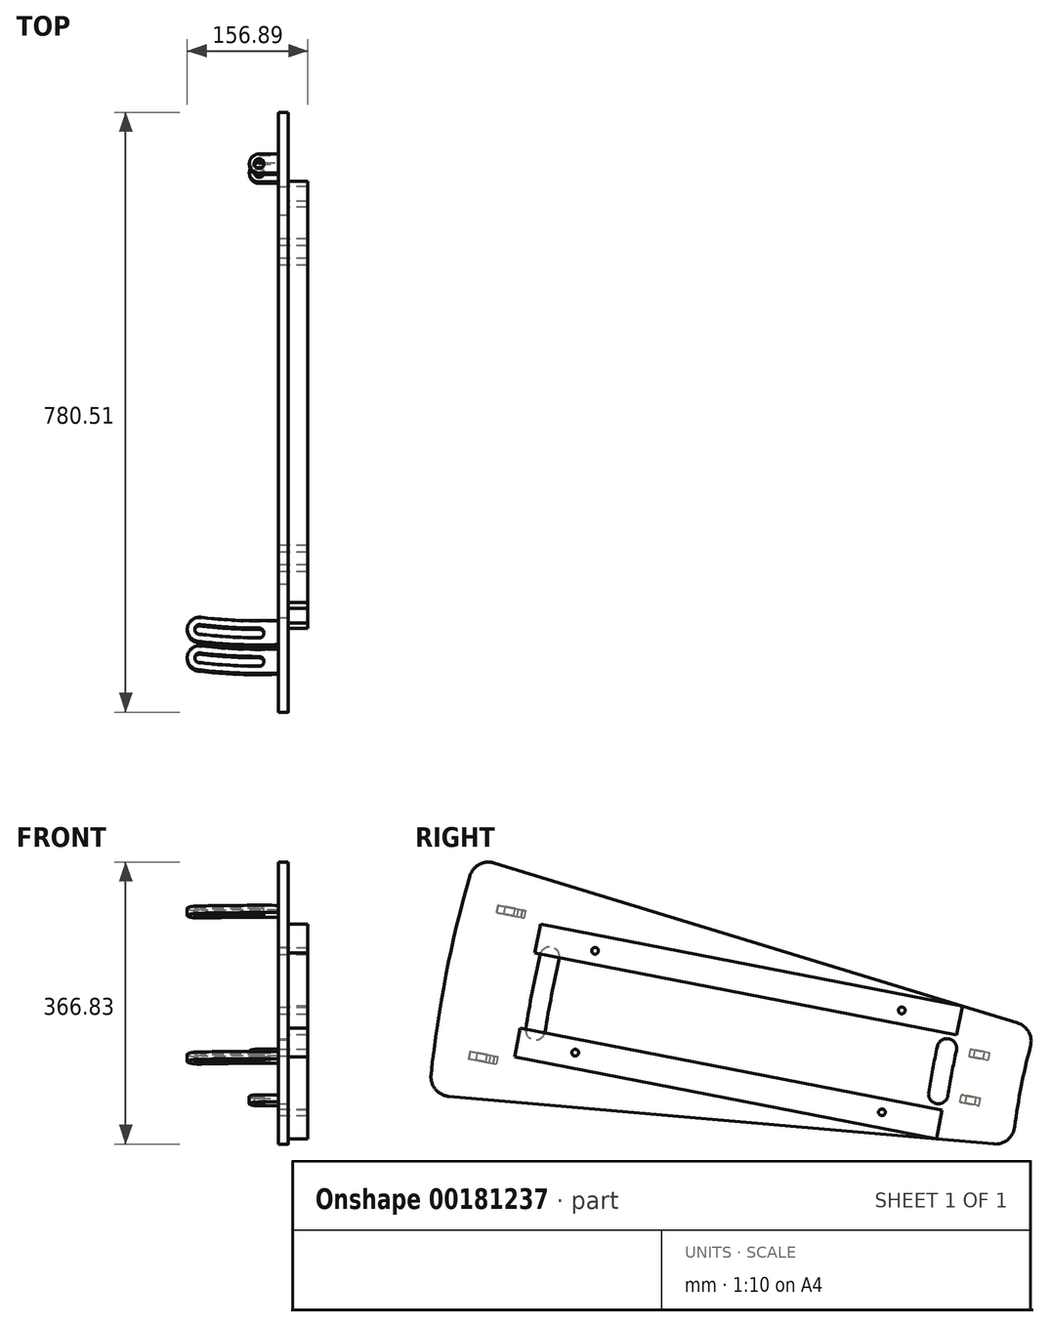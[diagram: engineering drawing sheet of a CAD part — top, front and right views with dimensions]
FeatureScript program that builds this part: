
annotation { "Feature Type Name" : "Feature", "Feature Type Description" : "" }
export const myFeature = defineFeature(function(context is Context, id is Id, definition is map)
    precondition{}
    {
        {
            var Q0;
            Q0=qCreatedBy(makeId("Right.planeOp"),FACE);
            var sketch = newSketch(context, id + "F0", { "sketchPlane" : qUnion([Q0])});
            skArc(sketch, "E0", {"start": v(-736.01, 197.3) * mm, "mid": v(-748, 145.4) * mm, "end": v(-756.33, 92.77) * mm});
            skLineSegment(sketch, "E1", {"start": v(0, 0) * mm, "end": v(-6.79, 0) * mm, "construction": true});
            skLineSegment(sketch, "E2", {"start": v(0, 0) * mm, "end": v(-1486.5, 288.95) * mm, "construction": true});
            skArc(sketch, "E3", {"start": v(-1465.3, 418.87) * mm, "mid": v(-1496, 290.8) * mm, "end": v(-1515.52, 160.55) * mm});
            skLineSegment(sketch, "E4", {"start": v(22.77, 0) * mm, "end": v(-18.63, 3.62) * mm});
            skArc(sketch, "E5", {"start": v(-844.59, 194.99) * mm, "mid": v(-850.72, 165.37) * mm, "end": v(-855.84, 135.55) * mm, "construction": true});
            skArc(sketch, "E6", {"start": v(-1361.2, 314.26) * mm, "mid": v(-1371.33, 266.56) * mm, "end": v(-1379.8, 218.54) * mm, "construction": true});
            skLineSegment(sketch, "E7.MirrorCS", {"start": v(21.1, -8.53) * mm, "end": v(-18.63, 3.62) * mm});
            skLineSegment(sketch, "E8.trimOffspring", {"start": v(-753.12, 228.18) * mm, "end": v(-1433.46, 436.18) * mm});
            skLineSegment(sketch, "E9.trimOffspring", {"start": v(-783.76, 70.56) * mm, "end": v(-1492.48, 132.57) * mm});
            skLineSegment(sketch, "E10.trimOffspring", {"start": v(-762, 0) * mm, "end": v(-1563.5, 0) * mm, "construction": true});
            skPoint(sketch, "E11.orphan", {"position": v(-1640.89, 499.6) * mm});
            skLineSegment(sketch, "E12", {"start": v(0, 0) * mm, "end": v(-1555.73, 246.4) * mm, "construction": true});
            skLineSegment(sketch, "E13", {"start": v(0, 0) * mm, "end": v(0, 0) * mm});
            skLineSegment(sketch, "E14.MirrorCS", {"start": v(0, 0) * mm, "end": v(-1534.75, 354.33) * mm, "construction": true});
            skArc(sketch, "E15.trimOffspring", {"start": v(-862.85, 77.48) * mm, "mid": v(-865.39, 38.78) * mm, "end": v(-866.23, 0) * mm, "construction": true});
            skArc(sketch, "E16.trimOffspring", {"start": v(-1391.5, 123.73) * mm, "mid": v(1371.33, -266.56) * mm, "end": v(-1336.54, 406.55) * mm, "construction": true});
            skArc(sketch, "E17.0.startCap", {"start": v(-1373.57, 317.11) * mm, "mid": v(-1358.34, 326.63) * mm, "end": v(-1348.82, 311.4) * mm});
            skArc(sketch, "E17.0.endCap", {"start": v(-1367.26, 216.55) * mm, "mid": v(-1381.79, 206) * mm, "end": v(-1392.34, 220.53) * mm});
            skArc(sketch, "E17.0.left", {"start": v(-1348.82, 311.4) * mm, "mid": v(-1358.87, 264.14) * mm, "end": v(-1367.26, 216.55) * mm});
            skArc(sketch, "E17.0.right", {"start": v(-1373.57, 317.11) * mm, "mid": v(-1383.8, 268.98) * mm, "end": v(-1392.34, 220.53) * mm});
            skArc(sketch, "E18.0.startCap", {"start": v(-856.98, 197.77) * mm, "mid": v(-841.8, 207.38) * mm, "end": v(-832.2, 192.2) * mm});
            skArc(sketch, "E18.0.endCap", {"start": v(-843.29, 133.62) * mm, "mid": v(-857.78, 123) * mm, "end": v(-868.4, 137.49) * mm});
            skArc(sketch, "E18.0.left", {"start": v(-832.2, 192.2) * mm, "mid": v(-838.24, 163) * mm, "end": v(-843.29, 133.62) * mm});
            skArc(sketch, "E18.0.right", {"start": v(-856.98, 197.77) * mm, "mid": v(-863.2, 167.73) * mm, "end": v(-868.4, 137.49) * mm});
            skPoint(sketch, "E19.visualSharp", {"position": v(-1457.99, 443.68) * mm});
            skArc(sketch, "E19.filletArc", {"start": v(-1433.46, 436.18) * mm, "mid": v(-1453.01, 434.2) * mm, "end": v(-1465.3, 418.87) * mm});
            skPoint(sketch, "E20.visualSharp", {"position": v(-729.28, 220.89) * mm});
            skArc(sketch, "E20.filletArc", {"start": v(-736.01, 197.3) * mm, "mid": v(-738.33, 216.2) * mm, "end": v(-753.12, 228.18) * mm});
            skPoint(sketch, "E21.visualSharp", {"position": v(-758.92, 68.39) * mm});
            skArc(sketch, "E21.filletArc", {"start": v(-783.76, 70.56) * mm, "mid": v(-765.56, 76.13) * mm, "end": v(-756.33, 92.77) * mm});
            skPoint(sketch, "E22.newPointA", {"position": v(-1708.56, 151.47) * mm});
            skArc(sketch, "E22.filletArc", {"start": v(-1515.52, 160.55) * mm, "mid": v(-1509.87, 141.72) * mm, "end": v(-1492.48, 132.57) * mm});
            skSolve(sketch);
        }
        {
            var Q0;
            Q0=makeQuery(id+"F0.imprint","IMPRINT",FACE,{"disambiguationData":[TD([[makeQuery(id+"F0.imprint","IMPRINT",EDGE,{"derivedFrom":sQuery(id+"F0.wireOp",EDGE,"E0")}),-1.0]])]});
            var Q1;
            Q1=makeQuery(id+"F0.imprint","IMPRINT",FACE,{"disambiguationData":[TD([[makeQuery(id+"F0.imprint","IMPRINT",EDGE,{"derivedFrom":sQuery(id+"F0.wireOp",EDGE,"E17.0.startCap")}),-1.0]])]});
            var Q2;
            Q2=makeQuery(id+"F0.imprint","IMPRINT",FACE,{"disambiguationData":[TD([[makeQuery(id+"F0.imprint","IMPRINT",EDGE,{"derivedFrom":sQuery(id+"F0.wireOp",EDGE,"E18.0.startCap")}),-1.0]])]});
            extrude(context, id + "F1", {"entities" : qUnion([Q0, Q1, Q2]), "oppositeDirection" : true, "depth" : 12.7 * mm});
        }
        {
            var Q0;
            Q0=makeQuery(id+"F1.opExtrude","SWEPT_FACE",FACE,{"disambiguationData":[OSD([sQuery(id+"F0.wireOp",EDGE,"E9.trimOffspring")])]});
            var Q1;
            Q1=makeQuery(id+"F1.opExtrude","SWEPT_FACE",FACE,{"disambiguationData":[OSD([sQuery(id+"F0.wireOp",EDGE,"E8.trimOffspring")])]});
            cPlane(context, id + "F2", {"entities" : qUnion([Q0, Q1]), "cplaneType" : CPlaneType.MID_PLANE, "offset" : 25.4 * mm, "width" : 152.4 * mm, "height" : 152.4 * mm});
        }
        {
            var Q0;
            Q0=qCreatedBy(id+"F2.planeOp",FACE);
            var sketch = newSketch(context, id + "F3", { "sketchPlane" : qUnion([Q0])});
            skLineSegment(sketch, "E23.0", {"start": v(-12.7, 782.82) * mm, "end": v(-12.7, 1490.35) * mm, "construction": true});
            skLineSegment(sketch, "E24", {"start": v(0, 760.08) * mm, "end": v(-12.7, 760.08) * mm, "construction": true});
            skLineSegment(sketch, "E25", {"start": v(-12.7, 760.08) * mm, "end": v(-65.49, 760.08) * mm, "construction": true});
            skLineSegment(sketch, "E26.0", {"start": v(-12.7, 823.58) * mm, "end": v(-38.1, 823.58) * mm, "construction": true});
            skCircle(sketch, "E27", {"center": v(-38.1, 823.58) * mm, "radius": 6.35 * mm});
            skCircle(sketch, "E28", {"center": v(-38.1, 823.58) * mm, "radius": 12.7 * mm});
            skLineSegment(sketch, "E29", {"start": v(-38.1, 829.93) * mm, "end": v(-38.1, 836.28) * mm});
            skLineSegment(sketch, "E30", {"start": v(-38.1, 836.28) * mm, "end": v(-12.7, 836.28) * mm});
            skLineSegment(sketch, "E31", {"start": v(-38.1, 817.23) * mm, "end": v(-38.1, 810.88) * mm});
            skLineSegment(sketch, "E32", {"start": v(-38.1, 810.88) * mm, "end": v(-12.7, 810.88) * mm});
            skLineSegment(sketch, "E33", {"start": v(-12.7, 810.88) * mm, "end": v(-12.7, 836.28) * mm});
            skSolve(sketch);
        }
        {
            var Q0;
            Q0=qSketchRegion(id+"F3",true);
            extrude(context, id + "F4", {"entities" : qUnion([Q0]), "operationType" : NewBodyOperationType.ADD, "endBound" : BoundingType.SYMMETRIC, "depth" : 50.8 * mm});
        }
        {
            var Q0;
            Q0=qCreatedBy(id+"F2.planeOp",FACE);
            cPlane(context, id + "F5", {"entities" : qUnion([Q0]), "cplaneType" : CPlaneType.OFFSET, "offset" : 101.6 * mm, "width" : 152.4 * mm, "height" : 152.4 * mm});
        }
        {
            var Q0;
            Q0=qCreatedBy(id+"F5.planeOp",FACE);
            var sketch = newSketch(context, id + "F6", { "sketchPlane" : qUnion([Q0])});
            skLineSegment(sketch, "E34.0.0", {"start": v(-12.7, 836.28) * mm, "end": v(-38.1, 836.28) * mm, "construction": true});
            skArc(sketch, "E34.0.1", {"start": v(-38.1, 836.28) * mm, "mid": v(-50.8, 823.58) * mm, "end": v(-38.1, 810.88) * mm, "construction": true});
            skLineSegment(sketch, "E34.0.2", {"start": v(-38.1, 810.88) * mm, "end": v(-12.7, 810.88) * mm, "construction": true});
            skLineSegment(sketch, "E34.0.3", {"start": v(-12.7, 810.88) * mm, "end": v(-12.7, 836.28) * mm, "construction": true});
            skLineSegment(sketch, "E35.0", {"start": v(0, 1518.3) * mm, "end": v(0, 1524) * mm, "construction": true});
            skLineSegment(sketch, "E35.3", {"start": v(0, 1490.35) * mm, "end": v(0, 1518.3) * mm, "construction": true});
            skLineSegment(sketch, "E35.4", {"start": v(0, 1383.45) * mm, "end": v(0, 1408.84) * mm, "construction": true});
            skLineSegment(sketch, "E35.5", {"start": v(0, 1518.3) * mm, "end": v(0, 1490.35) * mm, "construction": true});
            skLineSegment(sketch, "E35.6", {"start": v(0, 1408.84) * mm, "end": v(0, 1383.45) * mm, "construction": true});
            skLineSegment(sketch, "E35.10", {"start": v(12.7, 1383.45) * mm, "end": v(12.7, 1408.84) * mm, "construction": true});
            skLineSegment(sketch, "E35.11", {"start": v(-12.7, 1490.35) * mm, "end": v(0, 1490.35) * mm, "construction": true});
            skLineSegment(sketch, "E35.12", {"start": v(-12.7, 1518.3) * mm, "end": v(-12.7, 1490.35) * mm, "construction": true});
            skLineSegment(sketch, "E35.13", {"start": v(-12.7, 782.82) * mm, "end": v(-12.7, 836.28) * mm, "construction": true});
            skLineSegment(sketch, "E35.14", {"start": v(-12.7, 1518.3) * mm, "end": v(-12.7, 1524) * mm, "construction": true});
            skLineSegment(sketch, "E35.15", {"start": v(0, 1389.55) * mm, "end": v(0, -1397) * mm, "construction": true});
            skLineSegment(sketch, "E35.17", {"start": v(12.7, 1408.84) * mm, "end": v(0, 1408.84) * mm, "construction": true});
            skLineSegment(sketch, "E35.18", {"start": v(-12.7, 1518.3) * mm, "end": v(0, 1518.3) * mm, "construction": true});
            skLineSegment(sketch, "E35.19", {"start": v(0, 1518.3) * mm, "end": v(0, 1524) * mm, "construction": true});
            skLineSegment(sketch, "E35.20", {"start": v(-12.7, 1390.4) * mm, "end": v(-12.7, 1401.9) * mm, "construction": true});
            skLineSegment(sketch, "E35.21", {"start": v(12.7, 1401.9) * mm, "end": v(12.7, 1390.4) * mm, "construction": true});
            skLineSegment(sketch, "E35.22", {"start": v(12.7, 1401.9) * mm, "end": v(12.7, 1390.4) * mm, "construction": true});
            skLineSegment(sketch, "E35.23", {"start": v(-12.7, 1490.35) * mm, "end": v(-12.7, 1518.3) * mm, "construction": true});
            skLineSegment(sketch, "E35.24", {"start": v(-12.7, 1390.4) * mm, "end": v(-12.7, 1401.9) * mm, "construction": true});
            skLineSegment(sketch, "E35.25", {"start": v(12.7, 1408.84) * mm, "end": v(12.7, 1383.45) * mm, "construction": true});
            skLineSegment(sketch, "E35.26", {"start": v(-12.7, 1518.3) * mm, "end": v(0, 1518.3) * mm, "construction": true});
            skLineSegment(sketch, "E35.27", {"start": v(-12.7, 782.82) * mm, "end": v(-12.7, 1390.4) * mm, "construction": true});
            skLineSegment(sketch, "E35.29", {"start": v(-12.7, 1490.35) * mm, "end": v(0, 1490.35) * mm, "construction": true});
            skLineSegment(sketch, "E35.30", {"start": v(0, 1518.3) * mm, "end": v(0, 1490.35) * mm, "construction": true});
            skLineSegment(sketch, "E35.31", {"start": v(12.7, 1383.46) * mm, "end": v(0, 1383.46) * mm, "construction": true});
            skLineSegment(sketch, "E35.32", {"start": v(12.7, 1408.84) * mm, "end": v(12.7, 1409.7) * mm, "construction": true});
            skLineSegment(sketch, "E35.33", {"start": v(0, 1396.15) * mm, "end": v(0, 1397) * mm, "construction": true});
            skLineSegment(sketch, "E35.34", {"start": v(0, 1383.46) * mm, "end": v(0, 1384.3) * mm, "construction": true});
            skLineSegment(sketch, "E35.35", {"start": v(0, 1408.84) * mm, "end": v(0, 1409.7) * mm, "construction": true});
            skLineSegment(sketch, "E35.37", {"start": v(12.7, 1383.46) * mm, "end": v(0, 1383.46) * mm, "construction": true});
            skLineSegment(sketch, "E35.38", {"start": v(12.7, 1408.84) * mm, "end": v(0, 1408.84) * mm, "construction": true});
            skLineSegment(sketch, "E35.39", {"start": v(0, 1490.35) * mm, "end": v(0, 1518.3) * mm, "construction": true});
            skLineSegment(sketch, "E35.40", {"start": v(12.7, 1383.46) * mm, "end": v(12.7, 1384.3) * mm, "construction": true});
            skLineSegment(sketch, "E35.41", {"start": v(0, 1383.45) * mm, "end": v(0, 1408.84) * mm, "construction": true});
            skLineSegment(sketch, "E35.42", {"start": v(0, 1408.84) * mm, "end": v(0, 1409.7) * mm, "construction": true});
            skLineSegment(sketch, "E35.43", {"start": v(0, 1383.46) * mm, "end": v(0, 1384.3) * mm, "construction": true});
            skLineSegment(sketch, "E35.44", {"start": v(0, 1408.84) * mm, "end": v(0, 1383.45) * mm, "construction": true});
            skArc(sketch, "E36", {"start": v(0, 189.72) * mm, "mid": v(596.87, 829.93) * mm, "end": v(-12.7, 1458.07) * mm, "construction": true});
            skLineSegment(sketch, "E37", {"start": v(-38.1, 823.58) * mm, "end": v(-38.1, 1674.01) * mm, "construction": true});
            skLineSegment(sketch, "E38", {"start": v(-38.1, 823.58) * mm, "end": v(-115.49, 1453.84) * mm, "construction": true});
            skArc(sketch, "E39", {"start": v(-38.1, 1452.23) * mm, "mid": v(-31.75, 1458.58) * mm, "end": v(-38.1, 1464.93) * mm});
            skArc(sketch, "E40", {"start": v(-116.26, 1460.14) * mm, "mid": v(-121.79, 1453.07) * mm, "end": v(-114.71, 1447.54) * mm});
            skArc(sketch, "E41.trimOffspring", {"start": v(-31.75, 1458.54) * mm, "mid": v(-76.87, 1457.4) * mm, "end": v(-121.79, 1453.04) * mm, "construction": true});
            skArc(sketch, "E42.0", {"start": v(-38.1, 1464.93) * mm, "mid": v(-77.25, 1463.73) * mm, "end": v(-116.26, 1460.14) * mm});
            skArc(sketch, "E43.0", {"start": v(-38.1, 1452.23) * mm, "mid": v(-76.48, 1451.05) * mm, "end": v(-114.71, 1447.54) * mm});
            skLineSegment(sketch, "E44.0.0", {"start": v(0, 782.82) * mm, "end": v(0, 1409.7) * mm});
            skLineSegment(sketch, "E44.0.1", {"start": v(0, 1490.35) * mm, "end": v(-12.7, 1490.35) * mm});
            skLineSegment(sketch, "E44.0.2", {"start": v(-12.7, 1474.08) * mm, "end": v(-12.7, 1458.07) * mm});
            skLineSegment(sketch, "E44.0.3", {"start": v(-12.7, 782.82) * mm, "end": v(0, 782.82) * mm});
            skArc(sketch, "E45.0", {"start": v(-117.44, 1469.72) * mm, "mid": v(-131.37, 1451.9) * mm, "end": v(-113.54, 1437.96) * mm});
            skArc(sketch, "E46.0", {"start": v(-12.7, 1442.05) * mm, "mid": v(-63.2, 1442.06) * mm, "end": v(-113.54, 1437.96) * mm});
            skArc(sketch, "E47.0", {"start": v(-12.7, 1474.08) * mm, "mid": v(-68.4, 1473.87) * mm, "end": v(-123.9, 1468.9) * mm});
            skPoint(sketch, "E35.8.start.orphan", {"position": v(0, 748) * mm});
            skLineSegment(sketch, "E48.trimOffspring", {"start": v(-12.7, 1442.05) * mm, "end": v(-12.7, 1458.07) * mm, "construction": true});
            skLineSegment(sketch, "E49.trimOffspring", {"start": v(-12.7, 1442.05) * mm, "end": v(-12.7, 1474.08) * mm});
            skLineSegment(sketch, "E50.trimOffspring", {"start": v(-12.7, 1401.9) * mm, "end": v(-12.7, 782.82) * mm});
            skSolve(sketch);
        }
        {
            var Q0;
            Q0=qSketchRegion(id+"F6",true);
            extrude(context, id + "F7", {"entities" : qUnion([Q0]), "oppositeDirection" : true, "depth" : 9.65 * mm});
        }
        {
            var Q0;
            Q0=makeQuery(id+"F7.opExtrude","SWEPT_BODY",BODY,{"disambiguationData":[OSD([sQuery(id+"F6.wireOp",EDGE,"E39"),sQuery(id+"F6.wireOp",EDGE,"E40"),sQuery(id+"F6.wireOp",EDGE,"E42.0"),sQuery(id+"F6.wireOp",EDGE,"E43.0"),sQuery(id+"F6.wireOp",EDGE,"E45.0"),sQuery(id+"F6.wireOp",EDGE,"E46.0"),sQuery(id+"F6.wireOp",EDGE,"E47.0"),sQuery(id+"F6.wireOp",EDGE,"E49.trimOffspring")])]});
            var Q1;
            Q1=qCreatedBy(id+"F2.planeOp",FACE);
            mirror(context, id + "F8", {"entities" : qUnion([Q0]), "mirrorPlane" : qUnion([Q1])});
        }
        {
            var Q0;
            Q0=makeQuery(id+"F4.opExtrude","CAP_FACE",FACE,{"disambiguationData":[OSD([sQuery(id+"F3.wireOp",EDGE,"E27"),sQuery(id+"F3.wireOp",EDGE,"E28"),sQuery(id+"F3.wireOp",EDGE,"E30"),sQuery(id+"F3.wireOp",EDGE,"E32"),sQuery(id+"F3.wireOp",EDGE,"E33")])],"isStart":false});
            var sketch = newSketch(context, id + "F9", { "sketchPlane" : qUnion([Q0])});
            skLineSegment(sketch, "E51.0.0", {"start": v(-12.7, 836.28) * mm, "end": v(-38.1, 836.28) * mm});
            skArc(sketch, "E51.0.1", {"start": v(-38.1, 836.28) * mm, "mid": v(-50.8, 823.58) * mm, "end": v(-38.1, 810.88) * mm});
            skLineSegment(sketch, "E51.0.2", {"start": v(-38.1, 810.88) * mm, "end": v(-12.7, 810.88) * mm});
            skLineSegment(sketch, "E51.0.3", {"start": v(-12.7, 810.88) * mm, "end": v(-12.7, 836.28) * mm});
            skSolve(sketch);
        }
        {
            var Q0;
            Q0=qSketchRegion(id+"F9",true);
            extrude(context, id + "F10", {"entities" : qUnion([Q0]), "depth" : 9.65 * mm});
        }
        {
            var Q0;
            Q0=makeQuery(id+"F10.opExtrude","CAP_FACE",FACE,{"disambiguationData":[OSD([sQuery(id+"F9.wireOp",EDGE,"E51.0.0"),sQuery(id+"F9.wireOp",EDGE,"E51.0.1"),sQuery(id+"F9.wireOp",EDGE,"E51.0.2"),sQuery(id+"F9.wireOp",EDGE,"E51.0.3")])],"isStart":false});
            var sketch = newSketch(context, id + "F11", { "sketchPlane" : qUnion([Q0])});
            skCircle(sketch, "E52.0", {"center": v(-38.1, 823.58) * mm, "radius": 6.35 * mm});
            skSolve(sketch);
        }
        {
            var Q0;
            Q0=makeQuery(id+"F11.imprint","IMPRINT",FACE,{"disambiguationData":[TD([[makeQuery(id+"F11.imprint","IMPRINT",EDGE,{"derivedFrom":sQuery(id+"F11.wireOp",EDGE,"E52.0")}),1.0]])]});
            extrude(context, id + "F12", {"entities" : qUnion([Q0]), "operationType" : NewBodyOperationType.REMOVE, "oppositeDirection" : true, "depth" : 25.4 * mm});
        }
        {
            var Q0;
            Q0=makeQuery(id+"F4.opExtrude","SWEPT_FACE",FACE,{"disambiguationData":[OSD([sQuery(id+"F3.wireOp",EDGE,"E30")])]});
            var sketch = newSketch(context, id + "F13", { "sketchPlane" : qUnion([Q0])});
            skPoint(sketch, "E53.oppositeSnap0", {"position": v(-25.4, -25.4) * mm});
            skLineSegment(sketch, "E53.bottom", {"start": v(-12.7, 25.4) * mm, "end": v(-76.51, 25.4) * mm});
            skLineSegment(sketch, "E53.top", {"start": v(-12.7, -25.4) * mm, "end": v(-76.51, -25.4) * mm});
            skLineSegment(sketch, "E53.left", {"start": v(-12.7, 25.4) * mm, "end": v(-12.7, -25.4) * mm});
            skLineSegment(sketch, "E53.right", {"start": v(-76.51, 25.4) * mm, "end": v(-76.51, -25.4) * mm});
            skSolve(sketch);
        }
        {
            var Q0;
            Q0=qSketchRegion(id+"F13",true);
            extrude(context, id + "F14", {"entities" : qUnion([Q0]), "operationType" : NewBodyOperationType.REMOVE, "endBound" : BoundingType.THROUGH_ALL, "oppositeDirection" : true, "depth" : 25.4 * mm});
        }
        {
            var Q0;
            Q0=makeQuery(id+"F10.opExtrude","SWEPT_BODY",BODY,{"disambiguationData":[OSD([sQuery(id+"F9.wireOp",EDGE,"E51.0.0"),sQuery(id+"F9.wireOp",EDGE,"E51.0.1"),sQuery(id+"F9.wireOp",EDGE,"E51.0.2"),sQuery(id+"F9.wireOp",EDGE,"E51.0.3")])]});
            var Q1;
            Q1=qCreatedBy(id+"F2.planeOp",FACE);
            mirror(context, id + "F15", {"operationType" : NewBodyOperationType.ADD, "entities" : qUnion([Q0]), "mirrorPlane" : qUnion([Q1])});
        }
        {
            var Q0;
            Q0=qCreatedBy(id+"F2.planeOp",FACE);
            cPlane(context, id + "F16", {"entities" : qUnion([Q0]), "cplaneType" : CPlaneType.OFFSET, "offset" : 50 * mm, "width" : 152.4 * mm, "height" : 152.4 * mm});
        }
        {
            var Q0;
            Q0=qCreatedBy(id+"F16.planeOp",FACE);
            var sketch = newSketch(context, id + "F17", { "sketchPlane" : qUnion([Q0])});
            skLineSegment(sketch, "E54.0", {"start": v(0, 782.82) * mm, "end": v(0, 1490.35) * mm});
            skLineSegment(sketch, "E55.0", {"start": v(25.4, 857.18) * mm, "end": v(25.4, 1415.98) * mm});
            skLineSegment(sketch, "E56", {"start": v(25.4, 1136.58) * mm, "end": v(-165.05, 1136.58) * mm, "construction": true});
            skPoint(sketch, "E56.endSnap0", {"position": v(0, 1136.58) * mm});
            skLineSegment(sketch, "E57.0", {"start": v(25.4, 857.18) * mm, "end": v(0, 857.18) * mm});
            skPoint(sketch, "E58.orphan", {"position": v(25.4, 782.82) * mm});
            skLineSegment(sketch, "E59.MirrorCS", {"start": v(25.4, 1415.98) * mm, "end": v(0, 1415.98) * mm});
            skPoint(sketch, "E60.orphan", {"position": v(25.4, 1490.35) * mm});
            skSolve(sketch);
        }
        {
            var Q0;
            Q0=qSketchRegion(id+"F17",true);
            extrude(context, id + "F18", {"entities" : qUnion([Q0]), "depth" : 38.1 * mm});
        }
        {
            var Q0;
            Q0=makeQuery(id+"F18.opExtrude","SWEPT_BODY",BODY,{"disambiguationData":[OSD([sQuery(id+"F17.wireOp",EDGE,"E54.0"),sQuery(id+"F17.wireOp",EDGE,"E55.0"),sQuery(id+"F17.wireOp",EDGE,"E57.0"),sQuery(id+"F17.wireOp",EDGE,"E59.MirrorCS")])]});
            var Q1;
            Q1=qCreatedBy(id+"F2.planeOp",FACE);
            mirror(context, id + "F19", {"operationType" : NewBodyOperationType.ADD, "entities" : qUnion([Q0]), "mirrorPlane" : qUnion([Q1])});
        }
        {
            var Q0;
            Q0=makeQuery(id+"F19.opPattern","COPY",FACE,{"derivedFrom":makeQuery(id+"F18.opExtrude","SWEPT_FACE",FACE,{"disambiguationData":[OSD([sQuery(id+"F17.wireOp",EDGE,"E55.0")])]}),"instanceName":"1"});
            var sketch = newSketch(context, id + "F20", { "sketchPlane" : qUnion([Q0])});
            skLineSegment(sketch, "E61.0", {"start": v(0, 0) * mm, "end": v(-1486.5, 288.95) * mm, "construction": true});
            skLineSegment(sketch, "E62.0", {"start": v(12.88, 66.26) * mm, "end": v(-1473.63, 355.2) * mm, "construction": true});
            skLineSegment(sketch, "E63.0", {"start": v(-831.9, 212.64) * mm, "end": v(-1380.43, 319.26) * mm, "construction": true});
            skLineSegment(sketch, "E64", {"start": v(-1106.16, 265.95) * mm, "end": v(-1102.82, 283.13) * mm, "construction": true});
            skLineSegment(sketch, "E65.0", {"start": v(-906.7, 227.18) * mm, "end": v(-903.36, 244.36) * mm, "construction": true});
            skLineSegment(sketch, "E66.MirrorCS", {"start": v(-1305.63, 304.72) * mm, "end": v(-1302.29, 321.9) * mm, "construction": true});
            skPoint(sketch, "E67", {"position": v(-903.36, 244.36) * mm});
            skPoint(sketch, "E68", {"position": v(-1302.29, 321.9) * mm});
            skPoint(sketch, "E69.MirrorP", {"position": v(-929.12, 111.84) * mm});
            skPoint(sketch, "E70.MirrorP", {"position": v(-1328.05, 189.38) * mm});
            skSolve(sketch);
        }
        {
            var Q0;
            Q0=sQuery(id+"F20.wireOp",VERTEX,"E69.MirrorP");
            var Q1;
            Q1=sQuery(id+"F20.wireOp",VERTEX,"E70.MirrorP");
            var Q2;
            Q2=sQuery(id+"F20.wireOp",VERTEX,"E68");
            var Q3;
            Q3=sQuery(id+"F20.wireOp",VERTEX,"E67");
            var Q4;
            Q4=makeQuery(id+"F1.opExtrude","SWEPT_BODY",BODY,{"disambiguationData":[OSD([sQuery(id+"F0.wireOp",EDGE,"E0"),sQuery(id+"F0.wireOp",EDGE,"E3"),sQuery(id+"F0.wireOp",EDGE,"E8.trimOffspring"),sQuery(id+"F0.wireOp",EDGE,"E9.trimOffspring"),sQuery(id+"F0.wireOp",EDGE,"E19.filletArc"),sQuery(id+"F0.wireOp",EDGE,"E20.filletArc"),sQuery(id+"F0.wireOp",EDGE,"E21.filletArc"),sQuery(id+"F0.wireOp",EDGE,"E22.filletArc")])]});
            hole(context, id + "F21", {"style" : HoleStyle.SIMPLE, "endStyle" : HoleEndStyle.THROUGH, "standardTappedOrClearance" : lookupTablePath({ "standard" : "ISO", "fit" : "Normal", "size" : "M8", "type" : "Clearance" }), "standardBlindInLast" : lookupTablePath({ "fit" : "Standard", "standard" : "ISO", "size" : "M8", "type" : "Clearance" }), "holeDiameter" : 8.8 * mm, "locations" : qUnion([Q0, Q1, Q2, Q3]), "scope" : qUnion([Q4]), "isTappedThrough" : true});
        }
    });
